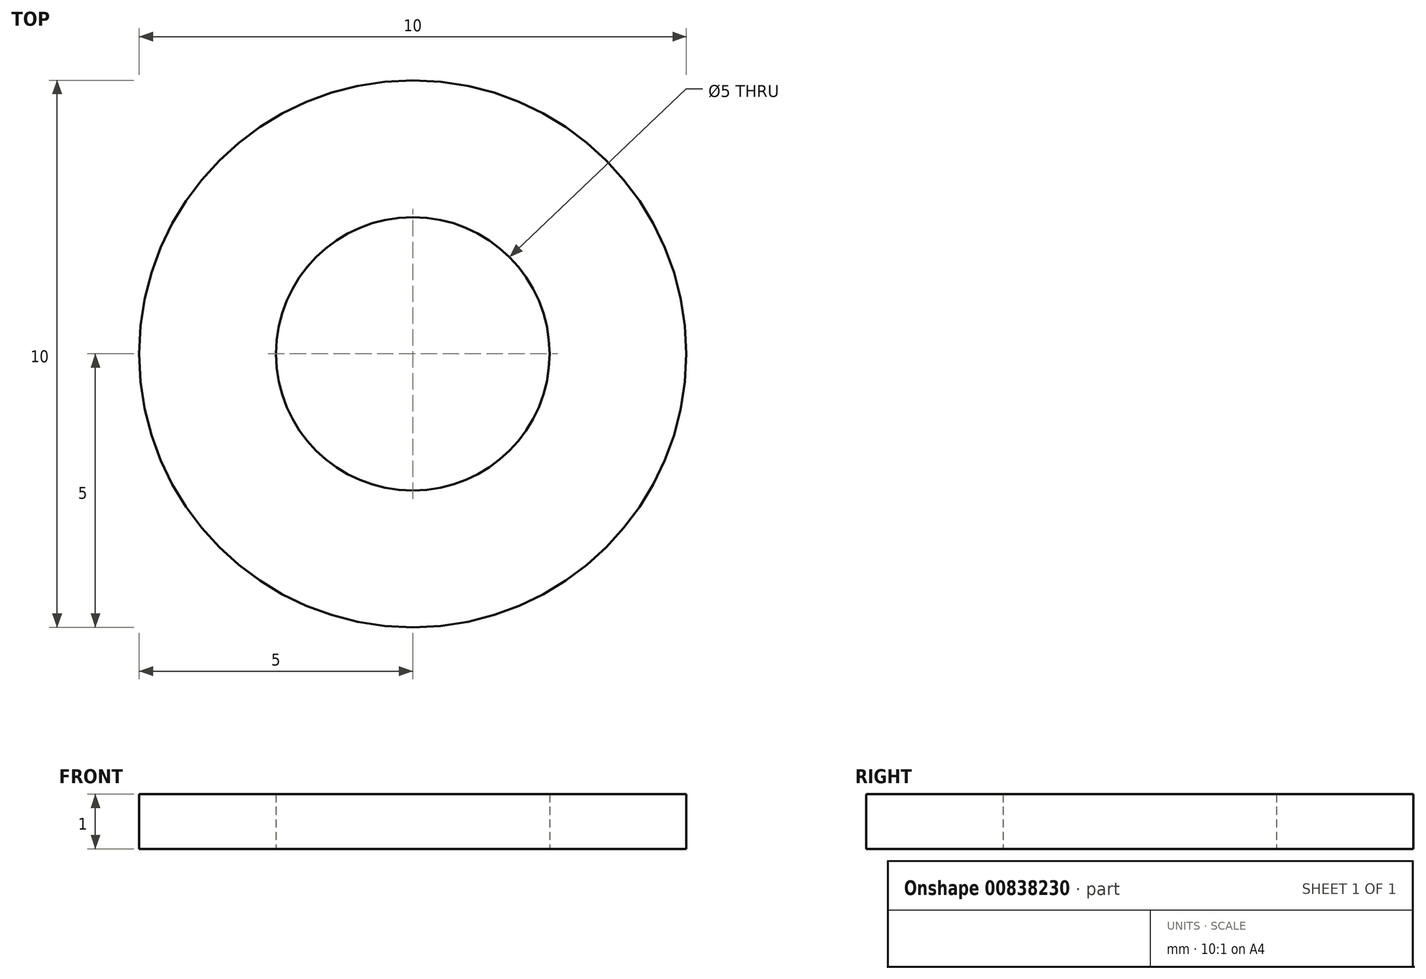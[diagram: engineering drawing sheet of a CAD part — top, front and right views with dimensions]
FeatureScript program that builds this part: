
annotation { "Feature Type Name" : "Feature", "Feature Type Description" : "" }
export const myFeature = defineFeature(function(context is Context, id is Id, definition is map)
    precondition{}
    {
        {
            var Q0;
            Q0=qCreatedBy(makeId("Top.planeOp"),FACE);
            var sketch = newSketch(context, id + "F0", { "sketchPlane" : qUnion([Q0])});
            skCircle(sketch, "E0", {"center": v(0, 0) * mm, "radius": 5 * mm});
            skCircle(sketch, "E1", {"center": v(0, 0) * mm, "radius": 2.5 * mm});
            skSolve(sketch);
        }
        {
            var Q0;
            Q0=qSketchRegion(id+"F0",true);
            extrude(context, id + "F1", {"entities" : qUnion([Q0]), "depth" : 1 * mm, "offsetDistance" : 25 * mm});
        }
    });
